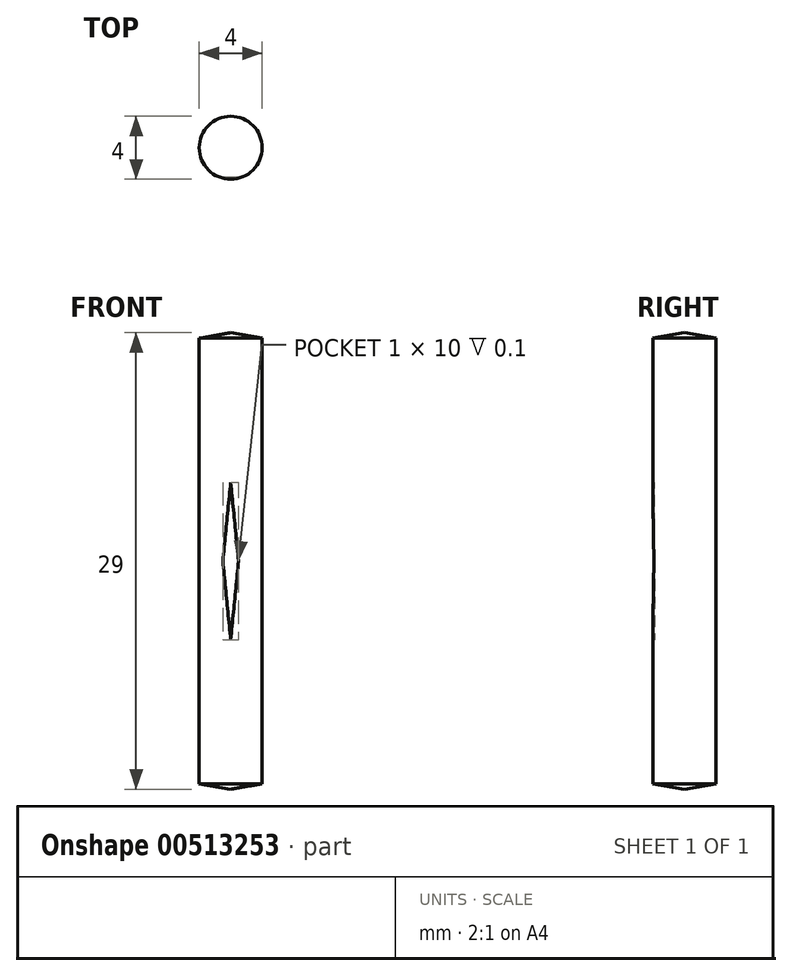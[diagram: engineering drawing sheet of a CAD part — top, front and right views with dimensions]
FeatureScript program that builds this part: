
annotation { "Feature Type Name" : "Feature", "Feature Type Description" : "" }
export const myFeature = defineFeature(function(context is Context, id is Id, definition is map)
    precondition{}
    {
        {
            var Q0;
            Q0=qCreatedBy(makeId("Top.planeOp"),FACE);
            var sketch = newSketch(context, id + "F0", { "sketchPlane" : qUnion([Q0])});
            skCircle(sketch, "E0", {"center": v(0, 0) * mm, "radius": 2 * mm});
            skSolve(sketch);
        }
        {
            var Q0;
            Q0 = qSketchRegion(id + "F0", true);
            extrude(context, id + "F1", {"entities" : qUnion([Q0]), "depth" : 29 * mm, "offsetDistance" : 25 * mm});
        }
        {
            var Q0;
            Q0=makeQuery(id+"F1.opExtrude","CAP_EDGE",EDGE,{"disambiguationData":[OSD([sQuery(id+"F0.wireOp",EDGE,"E0")])],"isStart":false});
            var Q1;
            Q1=makeQuery(id+"F1.opExtrude","CAP_EDGE",EDGE,{"disambiguationData":[OSD([sQuery(id+"F0.wireOp",EDGE,"E0")])],"isStart":true});
            chamfer(context, id + "F2", {"entities" : qUnion([Q0, Q1]), "chamferType" : ChamferType.OFFSET_ANGLE, "width" : 2 * mm, "oppositeDirection" : false, "angle" : 10 * degree, "tangentPropagation" : true});
        }
        {
            var Q0;
            Q0=qCreatedBy(makeId("Front.planeOp"),FACE);
            cPlane(context, id + "F3", {"entities" : qUnion([Q0]), "cplaneType" : CPlaneType.OFFSET, "offset" : 2 * mm, "width" : 150 * mm, "height" : 150 * mm});
        }
        {
            var Q0;
            Q0=qCreatedBy(id+"F3.planeOp",FACE);
            var sketch = newSketch(context, id + "F4", { "sketchPlane" : qUnion([Q0])});
            skLineSegment(sketch, "E1", {"start": v(0, 19.5) * mm, "end": v(-0.5, 14.5) * mm});
            skLineSegment(sketch, "E2", {"start": v(-0.5, 14.5) * mm, "end": v(0, 9.5) * mm});
            skLineSegment(sketch, "E3", {"start": v(0, 9.5) * mm, "end": v(0.5, 14.5) * mm});
            skLineSegment(sketch, "E4", {"start": v(0.5, 14.5) * mm, "end": v(0, 19.5) * mm});
            skSolve(sketch);
        }
        {
            var Q0;
            Q0 = qSketchRegion(id + "F4", true);
            extrude(context, id + "F5", {"entities" : qUnion([Q0]), "operationType" : NewBodyOperationType.REMOVE, "oppositeDirection" : true, "depth" : 0.1 * mm, "offsetDistance" : 25 * mm});
        }
    });
